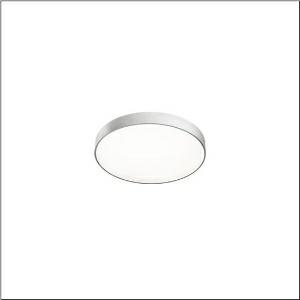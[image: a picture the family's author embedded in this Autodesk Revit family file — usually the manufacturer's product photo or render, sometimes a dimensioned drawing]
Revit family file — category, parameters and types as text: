
# Revit family: round_21_s_51mr34gd0321s
name_source: partatom
category: Lighting Fixtures
units: mm (PartAtom-declared; Revit-internal decimal feet)

## family parameters
Cut with Voids When Loaded = No
Host = Face
Light Source = No
Part Type = Normal
Room Calculation Point = No
Round Connector Dimension = Use Diameter
Shared = No

## types (1)
- Round 21 S (1 x LED, 3930 lm, 28.3 W, 3000K)
    Apparent Load = 28 VA
    CIE Flux Codes = 49 80 96 79 100
    Color Rendering = 80
    Color Temperature = 3000K
    Default Elevation = 1800 mm
    Description = Round 21 S, wall and ceiling luminaire, primary optical cover: cover, of PMMA, opal, light emission: direct/indirect distribution, primary light characteristic: symmetric, installation type: suspended mounting, surface-mounted, LED, rated luminous flux: 3.930lm, luminous efficacy: 139lm/W, light colour: 830, colour temperature: 3000K, control gear: DALI 2, with terminal, 5-pole, mains connection: 230V, AC, 50/60Hz, rated input power: 28.3W, housing, of aluminium, coated, silver, diameter: 400mm, height: 62mm, protection rating (complete): IP40, insulation class (complete): insulation class I (protective earthing), certification: CE, impact resistance: IK04, permissible operating ambient temperature: -10..+35°C, packaging unit: 1 piece
    Height = 87 mm
    Lamp = 1 x LED
    Lamp Light Flux = 3930 lm
    Lamp Power = 28.3 W
    Lamp count = 1
    Length = 400 mm
    Luminous efficacy = 139 lm/W
    Manufacturer = Siteco
    ModVariant = No
    Model = 51MR34GD0321S
    Mounting Place = Ceiling
    Mounting Type = Surface mounted
    Number of Poles = 1
    OnlyDefault = Yes
    Power Factor = 1
    Product Name = Round 21 S
    Product group = wall and ceiling luminaire
    ProductGroupID = 304
    Protection Class = Protection class I
    Protection Degree = IP 40
    RLX_Detail_Level = 1
    RLX_Emergency_Light_Flux = 0 lm
    RLX_Emergency_Type = 0
    RLX_Emergency_Type_DB = No
    RlxData = <blob elided: 11561 chars, md5=e958185a>
    Socket = socket
    Standby Power = 0 W
    System Light Flux = 3930 lm
    System Power = 28 W
    Type Comments = Product without accessories
    Type Image = l_1258309.jpg
    URL = http://relux.com
    VarID = ---
    Voltage = 0 V
    Weight = 0.00 kg
    Width = 0 mm  [stored 0 ft]

note: [stored X ft] marks values corroborated as IEEE doubles in the binary element streams (Revit-internal decimal feet)

## geometry (parser evidence)
native form markers: Sweep x11
no freeform markers — native parametric forms only
